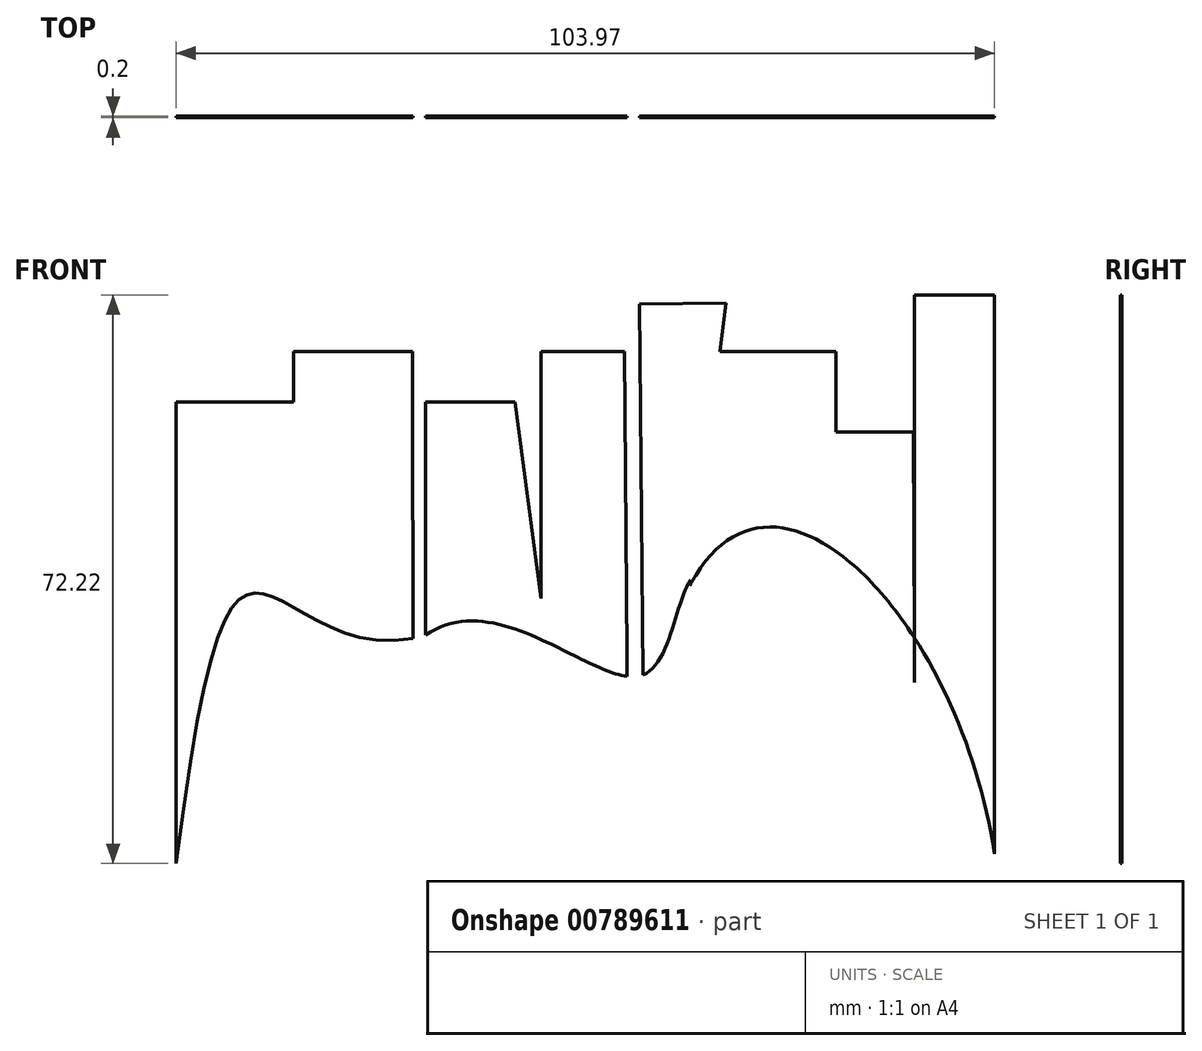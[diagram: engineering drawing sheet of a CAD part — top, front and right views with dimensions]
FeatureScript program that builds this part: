
annotation { "Feature Type Name" : "Feature", "Feature Type Description" : "" }
export const myFeature = defineFeature(function(context is Context, id is Id, definition is map)
    precondition{}
    {
        {
            var Q0;
            Q0=qCreatedBy(makeId("Front.planeOp"),FACE);
            var sketch = newSketch(context, id + "F0", { "sketchPlane" : qUnion([Q0])});
            skLineSegment(sketch, "E0", {"start": v(-51.76, 13.35) * mm, "end": v(-51.76, 71.93) * mm});
            skLineSegment(sketch, "E1", {"start": v(-51.76, 71.93) * mm, "end": v(-36.85, 71.93) * mm});
            skLineSegment(sketch, "E2", {"start": v(-36.85, 71.93) * mm, "end": v(-36.85, 47.02) * mm});
            skLineSegment(sketch, "E3", {"start": v(-36.85, 47.02) * mm, "end": v(-36.85, 78.35) * mm});
            skLineSegment(sketch, "E4", {"start": v(-36.85, 78.35) * mm, "end": v(-21.72, 78.35) * mm});
            skLineSegment(sketch, "E5", {"start": v(-21.72, 78.35) * mm, "end": v(-21.72, 47.02) * mm});
            skLineSegment(sketch, "E6", {"start": v(-21.72, 47.02) * mm, "end": v(-21.72, 71.93) * mm});
            skLineSegment(sketch, "E7", {"start": v(-5.4, 71.93) * mm, "end": v(-5.4, 47.02) * mm});
            skLineSegment(sketch, "E8", {"start": v(-5.4, 47.02) * mm, "end": v(-5.4, 78.35) * mm});
            skLineSegment(sketch, "E9", {"start": v(-5.4, 78.35) * mm, "end": v(5.2, 78.35) * mm});
            skLineSegment(sketch, "E10", {"start": v(7.13, 84.43) * mm, "end": v(18.09, 84.52) * mm});
            skLineSegment(sketch, "E11", {"start": v(18.09, 84.52) * mm, "end": v(13.52, 48.65) * mm});
            skLineSegment(sketch, "E12", {"start": v(13.52, 48.65) * mm, "end": v(17.3, 78.35) * mm});
            skLineSegment(sketch, "E13", {"start": v(17.3, 78.35) * mm, "end": v(32.06, 78.35) * mm});
            skLineSegment(sketch, "E14", {"start": v(32.06, 78.35) * mm, "end": v(32.06, 48.65) * mm});
            skLineSegment(sketch, "E15", {"start": v(32.06, 48.65) * mm, "end": v(32.06, 68.14) * mm});
            skLineSegment(sketch, "E16", {"start": v(32.06, 68.14) * mm, "end": v(41.93, 68.14) * mm});
            skLineSegment(sketch, "E17", {"start": v(41.93, 68.14) * mm, "end": v(42.03, 36.34) * mm});
            skLineSegment(sketch, "E18", {"start": v(42.03, 36.34) * mm, "end": v(42.03, 85.57) * mm});
            skLineSegment(sketch, "E19", {"start": v(52.21, 14.57) * mm, "end": v(52.21, 85.57) * mm});
            skLineSegment(sketch, "E20", {"start": v(52.21, 85.57) * mm, "end": v(42.03, 85.57) * mm});
            skLineSegment(sketch, "E21", {"start": v(7.13, 84.43) * mm, "end": v(7.52, 37.28) * mm});
            skLineSegment(sketch, "E22", {"start": v(5.2, 78.35) * mm, "end": v(5.53, 39.93) * mm});
            skLineSegment(sketch, "E23", {"start": v(5.53, 39.93) * mm, "end": v(5.23, 75.45) * mm});
            skLineSegment(sketch, "E24", {"start": v(-8.68, 71.93) * mm, "end": v(-5.4, 47.02) * mm});
            skLineSegment(sketch, "E25", {"start": v(-20.06, 71.93) * mm, "end": v(-20.06, 42.33) * mm});
            skLineSegment(sketch, "E26", {"start": v(-20.06, 71.93) * mm, "end": v(-8.68, 71.93) * mm});
            skFitSpline(sketch, "E27", {"points": [v(-51.76, 13.35) * mm, v(-20.06, 42.33) * mm], "startDerivative": vector(22.37, 175.75) * mm, "endDerivative": vector(61.68, 17.5) * mm});
            skFitSpline(sketch, "E28", {"points": [v(52.21, 14.57) * mm, v(13.52, 48.65) * mm], "startDerivative": vector(-13.78, 90.11) * mm, "endDerivative": vector(-31.97, -60.65) * mm});
            skFitSpline(sketch, "E29", {"points": [v(14.25, 49.94) * mm, v(7.52, 37.28) * mm, v(-20.06, 42.33) * mm], "startDerivative": vector(-18.07, -10.93) * mm, "endDerivative": vector(-48.7, -34.06) * mm});
            skLineSegment(sketch, "E30", {"start": v(-21.72, 47.02) * mm, "end": v(-21.68, 41.95) * mm});
            skLineSegment(sketch, "E31", {"start": v(-21.68, 41.95) * mm, "end": v(-21.72, 71.93) * mm});
            skLineSegment(sketch, "E32", {"start": v(-5.4, 47.02) * mm, "end": v(-4.66, 41.44) * mm});
            skLineSegment(sketch, "E33", {"start": v(-4.66, 41.44) * mm, "end": v(5.53, 37.1) * mm});
            skLineSegment(sketch, "E34", {"start": v(5.53, 39.93) * mm, "end": v(5.53, 37.1) * mm});
            skSolve(sketch);
        }
        {
            var Q0;
            Q0 = qSketchRegion(id + "F0", true);
            extrude(context, id + "F1", {"entities" : qUnion([Q0]), "depth" : 0.2 * mm, "offsetDistance" : 25 * mm});
        }
    });
